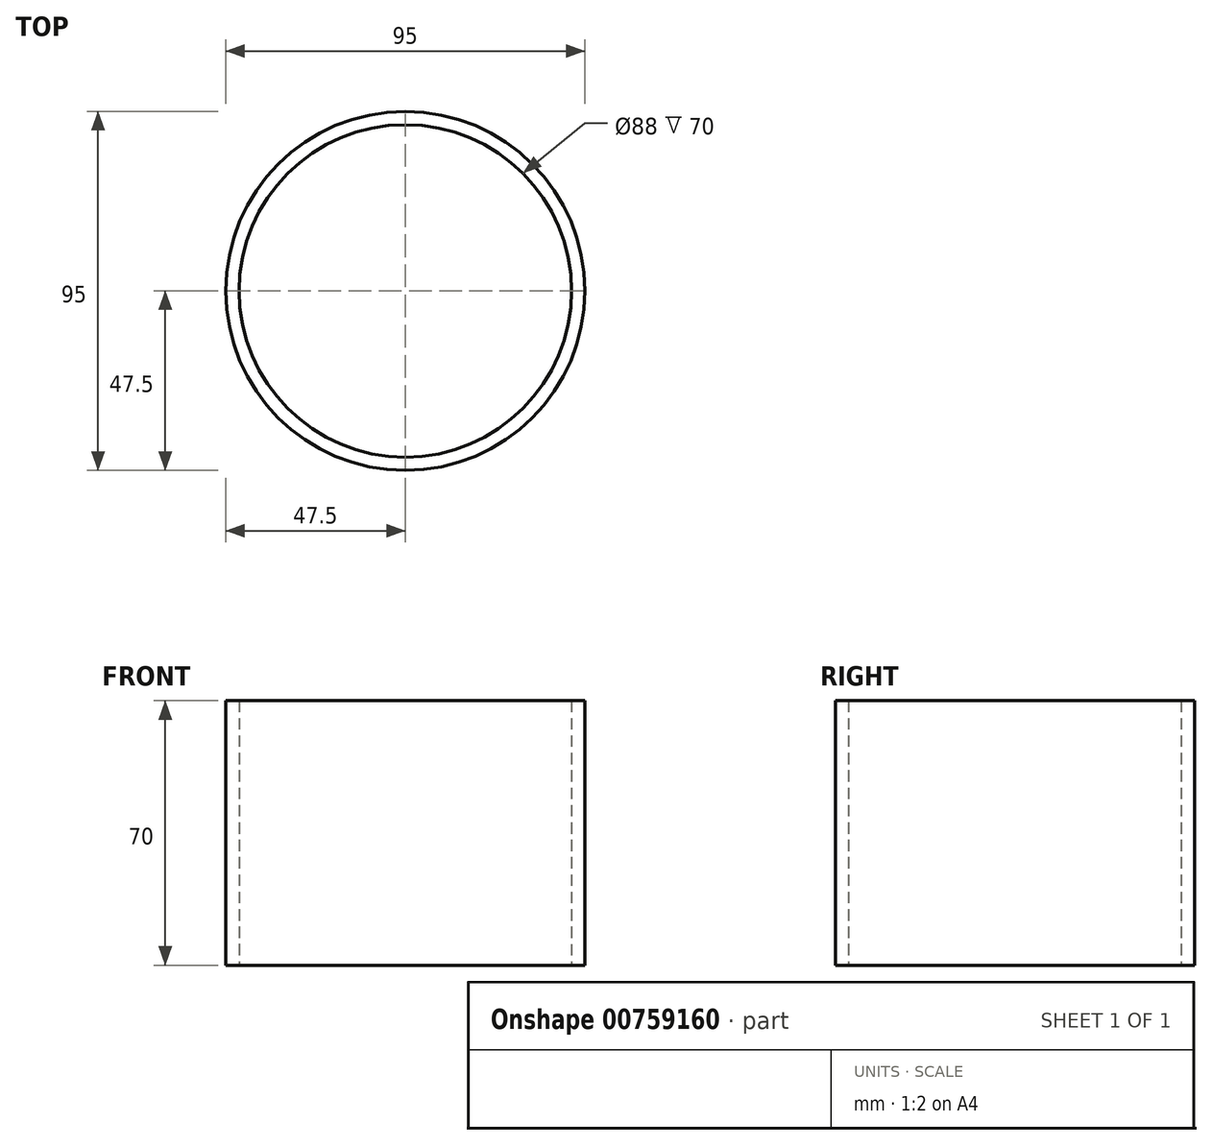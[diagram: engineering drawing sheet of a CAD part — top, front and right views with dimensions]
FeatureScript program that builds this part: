
annotation { "Feature Type Name" : "Feature", "Feature Type Description" : "" }
export const myFeature = defineFeature(function(context is Context, id is Id, definition is map)
    precondition{}
    {
        {
            var Q0;
            Q0=qCreatedBy(makeId("Top.planeOp"),FACE);
            var sketch = newSketch(context, id + "F0", { "sketchPlane" : qUnion([Q0])});
            skCircle(sketch, "E0", {"center": v(0, 0) * mm, "radius": 44 * mm});
            skCircle(sketch, "E1", {"center": v(0, 0) * mm, "radius": 47.5 * mm});
            skSolve(sketch);
        }
        {
            var Q0;
            Q0=makeQuery(id+"F0.imprint","IMPRINT",FACE,{"disambiguationData":[TD([[makeQuery(id+"F0.imprint","IMPRINT",EDGE,{"derivedFrom":sQuery(id+"F0.wireOp",EDGE,"E0")}),-1.0]])]});
            extrude(context, id + "F1", {"entities" : qUnion([Q0]), "depth" : 70 * mm, "offsetDistance" : 25 * mm});
        }
    });
